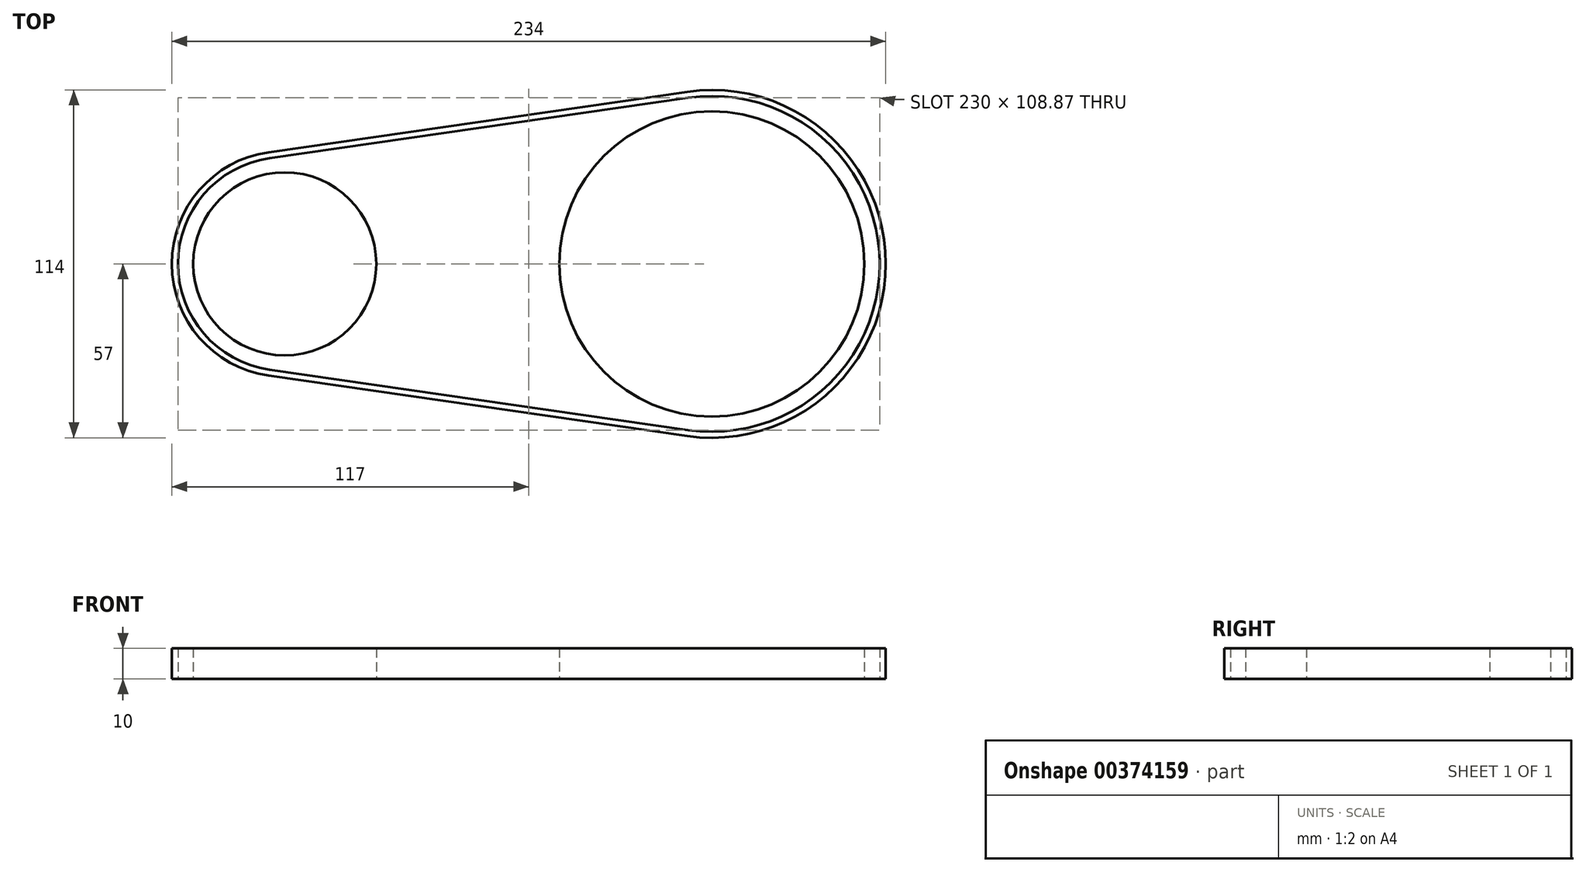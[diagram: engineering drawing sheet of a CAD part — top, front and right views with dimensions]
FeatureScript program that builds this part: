
annotation { "Feature Type Name" : "Feature", "Feature Type Description" : "" }
export const myFeature = defineFeature(function(context is Context, id is Id, definition is map)
    precondition{}
    {
        {
            var Q0;
            Q0=qCreatedBy(makeId("Top.planeOp"),FACE);
            var sketch = newSketch(context, id + "F0", { "sketchPlane" : qUnion([Q0])});
            skLineSegment(sketch, "E0", {"start": v(65.71, 0) * mm, "end": v(-74.29, 0) * mm, "construction": true});
            skCircle(sketch, "E1", {"center": v(-74.29, 0) * mm, "radius": 30 * mm});
            skCircle(sketch, "E2", {"center": v(65.71, 0) * mm, "radius": 50 * mm});
            skArc(sketch, "E3.0", {"start": v(-79.29, 34.64) * mm, "mid": v(-109.29, 0) * mm, "end": v(-79.29, -34.64) * mm});
            skArc(sketch, "E4.0", {"start": v(57.85, -54.44) * mm, "mid": v(120.71, 0) * mm, "end": v(57.85, 54.44) * mm});
            skLineSegment(sketch, "E5", {"start": v(-79.29, 34.64) * mm, "end": v(57.85, 54.44) * mm});
            skLineSegment(sketch, "E6.MirrorCS", {"start": v(-79.29, -34.64) * mm, "end": v(57.85, -54.44) * mm});
            skLineSegment(sketch, "E7.0", {"start": v(-79.58, 36.62) * mm, "end": v(57.57, 56.42) * mm});
            skArc(sketch, "E7.1", {"start": v(-79.58, 36.62) * mm, "mid": v(-111.29, 0) * mm, "end": v(-79.58, -36.62) * mm});
            skLineSegment(sketch, "E7.2", {"start": v(-79.58, -36.62) * mm, "end": v(57.57, -56.42) * mm});
            skArc(sketch, "E7.3", {"start": v(57.57, -56.42) * mm, "mid": v(122.71, 0) * mm, "end": v(57.57, 56.42) * mm});
            skSolve(sketch);
        }
        {
            var Q0;
            Q0=makeQuery(id+"F0.imprint","IMPRINT",FACE,{"disambiguationData":[TD([[makeQuery(id+"F0.imprint","IMPRINT",EDGE,{"derivedFrom":sQuery(id+"F0.wireOp",EDGE,"E3.0")}),-1.0]])]});
            var Q1;
            Q1=makeQuery(id+"F0.imprint","IMPRINT",FACE,{"disambiguationData":[TD([[makeQuery(id+"F0.imprint","IMPRINT",EDGE,{"derivedFrom":sQuery(id+"F0.wireOp",EDGE,"E1")}),1.0]])]});
            var Q2;
            Q2=makeQuery(id+"F0.imprint","IMPRINT",FACE,{"disambiguationData":[TD([[makeQuery(id+"F0.imprint","IMPRINT",EDGE,{"derivedFrom":sQuery(id+"F0.wireOp",EDGE,"E2")}),1.0]])]});
            extrude(context, id + "F1", {"entities" : qUnion([Q0, Q1, Q2]), "endBound" : BoundingType.SYMMETRIC, "depth" : 10 * mm});
        }
    });
